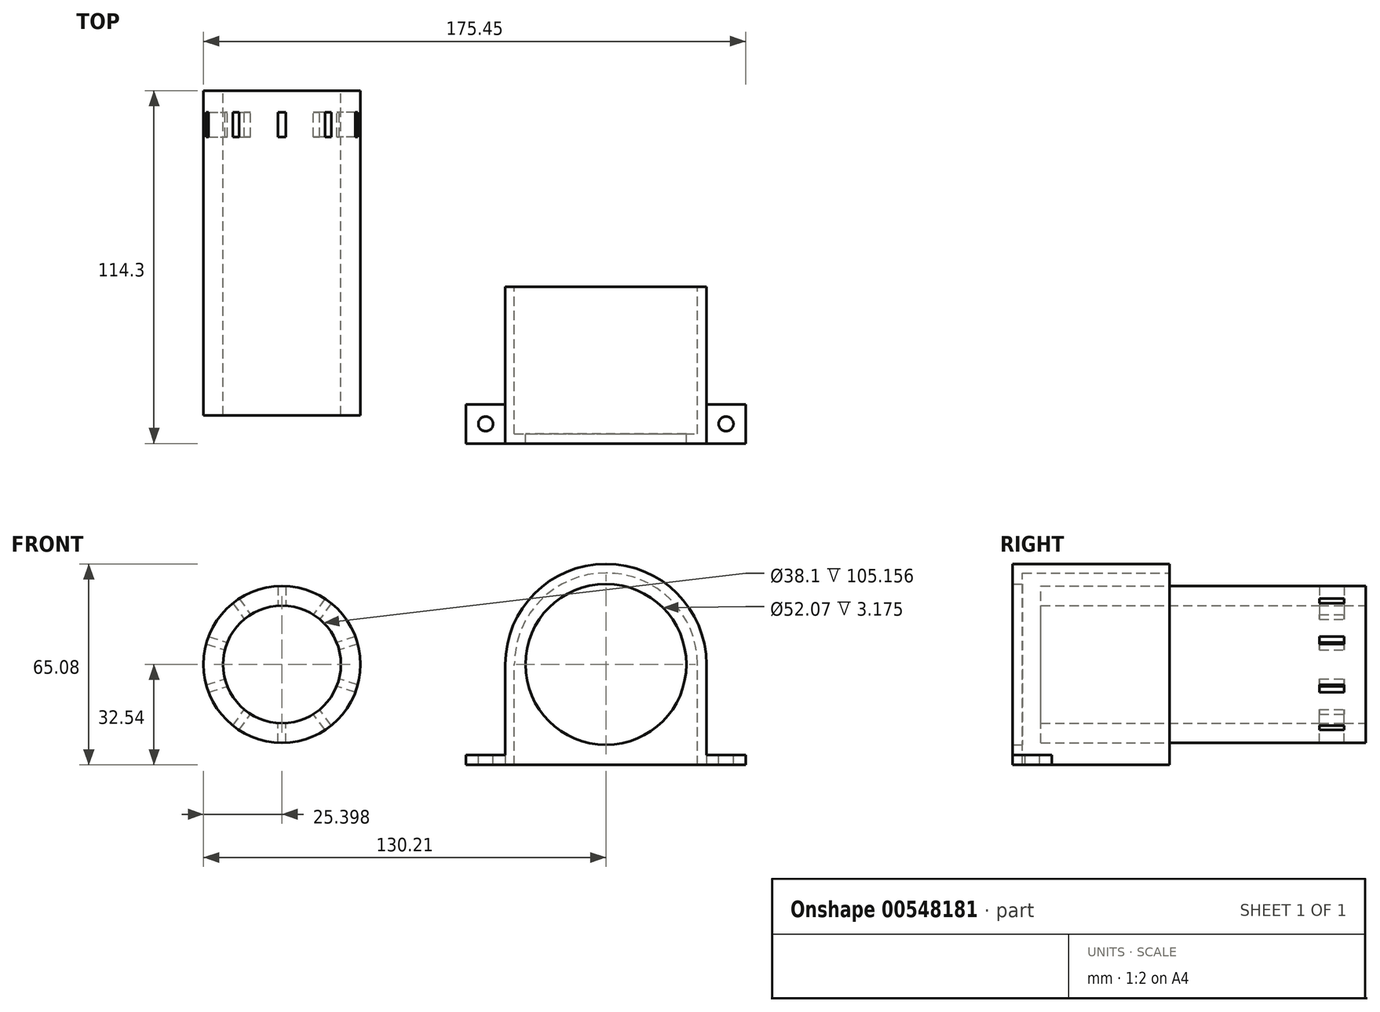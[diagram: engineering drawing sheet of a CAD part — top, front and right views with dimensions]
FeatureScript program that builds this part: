
annotation { "Feature Type Name" : "Feature", "Feature Type Description" : "" }
export const myFeature = defineFeature(function(context is Context, id is Id, definition is map)
    precondition{}
    {
        {
            var Q0;
            Q0=qCreatedBy(makeId("Front.planeOp"),FACE);
            var sketch = newSketch(context, id + "F0", { "sketchPlane" : qUnion([Q0])});
            skCircle(sketch, "E0", {"center": v(0, 0) * mm, "radius": 26.04 * mm});
            skLineSegment(sketch, "E1", {"start": v(0, -32.54) * mm, "end": v(32.54, -32.54) * mm});
            skLineSegment(sketch, "E2", {"start": v(32.54, -32.54) * mm, "end": v(32.54, 0) * mm});
            skLineSegment(sketch, "E3.MirrorCS", {"start": v(0, -32.54) * mm, "end": v(-32.54, -32.54) * mm});
            skLineSegment(sketch, "E4.MirrorCS", {"start": v(-32.54, -32.54) * mm, "end": v(-32.54, 0) * mm});
            skArc(sketch, "E5", {"start": v(32.54, 0) * mm, "mid": v(0, 32.54) * mm, "end": v(-32.54, 0) * mm});
            skSolve(sketch);
        }
        {
            var Q0;
            Q0 = qSketchRegion(id + "F0", true);
            extrude(context, id + "F1", {"entities" : qUnion([Q0]), "depth" : 114.3 * mm, "offsetDistance" : 25.4 * mm});
        }
        {
            var Q0;
            Q0=makeQuery(id+"F1.opExtrude","CAP_FACE",FACE,{"disambiguationData":[OSD([sQuery(id+"F0.wireOp",EDGE,"E0"),sQuery(id+"F0.wireOp",EDGE,"E1"),sQuery(id+"F0.wireOp",EDGE,"E2"),sQuery(id+"F0.wireOp",EDGE,"E3.MirrorCS"),sQuery(id+"F0.wireOp",EDGE,"E4.MirrorCS"),sQuery(id+"F0.wireOp",EDGE,"E5")])],"isStart":true});
            var sketch = newSketch(context, id + "F2", { "sketchPlane" : qUnion([Q0])});
            skCircle(sketch, "E6", {"center": v(0, 0) * mm, "radius": 29.62 * mm});
            skSolve(sketch);
        }
        {
            var Q0;
            Q0 = qSketchRegion(id + "F2", true);
            extrude(context, id + "F3", {"entities" : qUnion([Q0]), "operationType" : NewBodyOperationType.REMOVE, "oppositeDirection" : true, "depth" : 111.12 * mm, "offsetDistance" : 25.4 * mm});
        }
        {
            var Q0;
            Q0=makeQuery(id+"F1.opExtrude","CAP_FACE",FACE,{"disambiguationData":[OSD([sQuery(id+"F0.wireOp",EDGE,"E0"),sQuery(id+"F0.wireOp",EDGE,"E1"),sQuery(id+"F0.wireOp",EDGE,"E2"),sQuery(id+"F0.wireOp",EDGE,"E3.MirrorCS"),sQuery(id+"F0.wireOp",EDGE,"E4.MirrorCS"),sQuery(id+"F0.wireOp",EDGE,"E5")])],"isStart":true});
            var sketch = newSketch(context, id + "F4", { "sketchPlane" : qUnion([Q0])});
            skLineSegment(sketch, "E7.bottom", {"start": v(0, -50) * mm, "end": v(29.62, -50) * mm});
            skLineSegment(sketch, "E7.top", {"start": v(0, 0) * mm, "end": v(29.62, 0) * mm});
            skLineSegment(sketch, "E7.right", {"start": v(29.62, -50) * mm, "end": v(29.62, 0) * mm});
            skLineSegment(sketch, "E8.MirrorCS", {"start": v(0, 0) * mm, "end": v(-29.62, 0) * mm});
            skLineSegment(sketch, "E9.MirrorCS", {"start": v(-29.62, -50) * mm, "end": v(-29.62, 0) * mm});
            skLineSegment(sketch, "E10.MirrorCS", {"start": v(0, -50) * mm, "end": v(-29.62, -50) * mm});
            skSolve(sketch);
        }
        {
            var Q0;
            Q0 = qSketchRegion(id + "F4", true);
            extrude(context, id + "F5", {"entities" : qUnion([Q0]), "operationType" : NewBodyOperationType.REMOVE, "oppositeDirection" : true, "depth" : 111.12 * mm, "offsetDistance" : 25.4 * mm});
        }
        {
            var Q0;
            Q0=makeQuery(id+"F1.opExtrude","SWEPT_FACE",FACE,{"disambiguationData":[OSD([sQuery(id+"F0.wireOp",EDGE,"E1"),sQuery(id+"F0.wireOp",EDGE,"E3.MirrorCS")])]});
            var sketch = newSketch(context, id + "F6", { "sketchPlane" : qUnion([Q0])});
            skLineSegment(sketch, "E11.bottom", {"start": v(0, 114.3) * mm, "end": v(45.24, 114.3) * mm});
            skLineSegment(sketch, "E11.top", {"start": v(0, 101.6) * mm, "end": v(32.54, 101.6) * mm});
            skLineSegment(sketch, "E12", {"start": v(45.24, 114.3) * mm, "end": v(45.24, 101.6) * mm});
            skLineSegment(sketch, "E13", {"start": v(32.54, 101.6) * mm, "end": v(45.24, 101.6) * mm});
            skLineSegment(sketch, "E14.MirrorCS", {"start": v(0, 114.3) * mm, "end": v(-45.24, 114.3) * mm});
            skLineSegment(sketch, "E15.MirrorCS", {"start": v(-45.24, 114.3) * mm, "end": v(-45.24, 101.6) * mm});
            skLineSegment(sketch, "E16.MirrorCS", {"start": v(-32.54, 101.6) * mm, "end": v(-45.24, 101.6) * mm});
            skLineSegment(sketch, "E17.MirrorCS", {"start": v(0, 101.6) * mm, "end": v(-32.54, 101.6) * mm});
            skSolve(sketch);
        }
        {
            var Q0;
            Q0 = qSketchRegion(id + "F6", true);
            extrude(context, id + "F7", {"entities" : qUnion([Q0]), "operationType" : NewBodyOperationType.ADD, "oppositeDirection" : true, "depth" : 3.17 * mm, "offsetDistance" : 25.4 * mm});
        }
        {
            var Q0;
            Q0=makeQuery(id+"F7.boolean.opBoolean","MERGE",FACE,{"derivedFrom":[makeQuery(id+"F1.opExtrude","SWEPT_FACE",FACE,{"disambiguationData":[OSD([sQuery(id+"F0.wireOp",EDGE,"E1"),sQuery(id+"F0.wireOp",EDGE,"E3.MirrorCS")])]}),makeQuery(id+"F7.opExtrude","CAP_FACE",FACE,{"disambiguationData":[OSD([sQuery(id+"F6.wireOp",EDGE,"E11.bottom"),sQuery(id+"F6.wireOp",EDGE,"E11.top"),sQuery(id+"F6.wireOp",EDGE,"E12"),sQuery(id+"F6.wireOp",EDGE,"E13"),sQuery(id+"F6.wireOp",EDGE,"E14.MirrorCS"),sQuery(id+"F6.wireOp",EDGE,"E15.MirrorCS"),sQuery(id+"F6.wireOp",EDGE,"E16.MirrorCS"),sQuery(id+"F6.wireOp",EDGE,"E17.MirrorCS")])],"isStart":true})]});
            var sketch = newSketch(context, id + "F8", { "sketchPlane" : qUnion([Q0])});
            skLineSegment(sketch, "E18.bottom", {"start": v(-32.54, 50.8) * mm, "end": v(-45.24, 50.8) * mm});
            skLineSegment(sketch, "E18.top", {"start": v(-32.54, 63.5) * mm, "end": v(-45.24, 63.5) * mm});
            skLineSegment(sketch, "E18.left", {"start": v(-32.54, 50.8) * mm, "end": v(-32.54, 63.5) * mm});
            skLineSegment(sketch, "E18.right", {"start": v(-45.24, 50.8) * mm, "end": v(-45.24, 63.5) * mm});
            skLineSegment(sketch, "E19.MirrorCS", {"start": v(32.54, 50.8) * mm, "end": v(32.54, 63.5) * mm});
            skLineSegment(sketch, "E20.MirrorCS", {"start": v(32.54, 63.5) * mm, "end": v(45.24, 63.5) * mm});
            skLineSegment(sketch, "E21.MirrorCS", {"start": v(45.24, 50.8) * mm, "end": v(45.24, 63.5) * mm});
            skLineSegment(sketch, "E22.MirrorCS", {"start": v(32.54, 50.8) * mm, "end": v(45.24, 50.8) * mm});
            skSolve(sketch);
        }
        {
            var Q0;
            Q0 = qSketchRegion(id + "F8", true);
            extrude(context, id + "F9", {"entities" : qUnion([Q0]), "operationType" : NewBodyOperationType.ADD, "oppositeDirection" : true, "depth" : 3.17 * mm, "offsetDistance" : 25.4 * mm});
        }
        {
            var Q0;
            {var subQ0=sQuery(id+"F6.wireOp",EDGE,"E14.MirrorCS");var subQ1=sQuery(id+"F6.wireOp",EDGE,"E11.bottom");var subQ2=sQuery(id+"F0.wireOp",EDGE,"E2");var subQ3=sQuery(id+"F6.wireOp",EDGE,"E17.MirrorCS");var subQ4=sQuery(id+"F6.wireOp",EDGE,"E16.MirrorCS");var subQ5=sQuery(id+"F6.wireOp",EDGE,"E13");var subQ6=sQuery(id+"F6.wireOp",EDGE,"E11.top");var subQ7=sQuery(id+"F6.wireOp",EDGE,"E12");Q0=makeQuery(id+"F7.boolean.opBoolean","SPLIT",FACE,{"disambiguationData":[TD([makeQuery(id+"F1.opExtrude","SWEPT_FACE",FACE,{"disambiguationData":[OSD([subQ2])]})])],"derivedFrom":makeQuery(id+"F7.opExtrude","CAP_FACE",FACE,{"disambiguationData":[OSD([subQ1,subQ6,subQ7,subQ5,subQ0,sQuery(id+"F6.wireOp",EDGE,"E15.MirrorCS"),subQ4,subQ3])],"isStart":false})});}
            var sketch = newSketch(context, id + "F10", { "sketchPlane" : qUnion([Q0])});
            skCircle(sketch, "E23", {"center": v(-38.9, -57.15) * mm, "radius": 2.38 * mm});
            skCircle(sketch, "E24", {"center": v(-38.9, -107.95) * mm, "radius": 2.38 * mm});
            skCircle(sketch, "E25", {"center": v(38.9, -57.15) * mm, "radius": 2.38 * mm});
            skCircle(sketch, "E26", {"center": v(38.9, -107.95) * mm, "radius": 2.38 * mm});
            skSolve(sketch);
        }
        {
            var Q0;
            Q0 = qSketchRegion(id + "F10", true);
            extrude(context, id + "F11", {"entities" : qUnion([Q0]), "operationType" : NewBodyOperationType.REMOVE, "oppositeDirection" : true, "depth" : 25.4 * mm, "offsetDistance" : 25.4 * mm});
        }
        {
            var Q0;
            Q0=qCreatedBy(makeId("Front.planeOp"),FACE);
            var sketch = newSketch(context, id + "F12", { "sketchPlane" : qUnion([Q0])});
            skCircle(sketch, "E27", {"center": v(-104.81, 0) * mm, "radius": 25.4 * mm});
            skCircle(sketch, "E28", {"center": v(-104.81, 0) * mm, "radius": 19.05 * mm});
            skSolve(sketch);
        }
        {
            var Q0;
            Q0 = qSketchRegion(id + "F12", true);
            extrude(context, id + "F13", {"entities" : qUnion([Q0]), "depth" : 105.16 * mm, "offsetDistance" : 25.4 * mm});
        }
        {
            var Q0;
            Q0=qCreatedBy(makeId("Top.planeOp"),FACE);
            var sketch = newSketch(context, id + "F14", { "sketchPlane" : qUnion([Q0])});
            skLineSegment(sketch, "E29.bottom", {"start": v(-106.09, -7.03) * mm, "end": v(-103.55, -7.03) * mm});
            skLineSegment(sketch, "E29.top", {"start": v(-106.09, -15) * mm, "end": v(-103.55, -15) * mm});
            skLineSegment(sketch, "E29.left", {"start": v(-106.09, -7.03) * mm, "end": v(-106.09, -15) * mm});
            skLineSegment(sketch, "E29.right", {"start": v(-103.55, -7.03) * mm, "end": v(-103.55, -15) * mm});
            skSolve(sketch);
        }
        {
            var Q0;
            Q0 = qSketchRegion(id + "F14", true);
            extrude(context, id + "F15", {"entities" : qUnion([Q0]), "oppositeDirection" : true, "depth" : 32.77 * mm, "offsetDistance" : 25.4 * mm});
        }
        {
            var Q0;
            Q0=makeQuery(id+"F15.opExtrude","SWEPT_BODY",BODY,{"disambiguationData":[OSD([sQuery(id+"F14.wireOp",EDGE,"E29.bottom"),sQuery(id+"F14.wireOp",EDGE,"E29.top"),sQuery(id+"F14.wireOp",EDGE,"E29.left"),sQuery(id+"F14.wireOp",EDGE,"E29.right")])]});
            var Q1;
            Q1=makeQuery(id+"F13.opExtrude","CAP_EDGE",EDGE,{"disambiguationData":[OSD([sQuery(id+"F12.wireOp",EDGE,"E28")])],"isStart":true});
            circularPattern(context, id + "F16", {"operationType" : NewBodyOperationType.REMOVE, "entities" : qUnion([Q0]), "axis" : qUnion([Q1]), "angle" : 360 * degree, "instanceCount" : 10, "equalSpace" : true, "computeTransformsWithoutBuiltin" : true});
        }
        {
            var Q0;
            {var subQ2=sQuery(id+"F6.wireOp",EDGE,"E17.MirrorCS");var subQ3=sQuery(id+"F6.wireOp",EDGE,"E16.MirrorCS");var subQ4=sQuery(id+"F6.wireOp",EDGE,"E13");var subQ5=sQuery(id+"F6.wireOp",EDGE,"E11.top");Q0=makeQuery(id+"F7.boolean.opBoolean","SPLIT",FACE,{"disambiguationData":[TD([makeQuery(id+"F3.boolean.opBoolean","COPY",FACE,{"derivedFrom":makeQuery(id+"F3.opExtrude","CAP_FACE",FACE,{"disambiguationData":[OSD([sQuery(id+"F2.wireOp",EDGE,"E6")])],"isStart":false})})])],"derivedFrom":makeQuery(id+"F7.opExtrude","CAP_FACE",FACE,{"disambiguationData":[OSD([sQuery(id+"F6.wireOp",EDGE,"E11.bottom"),subQ5,sQuery(id+"F6.wireOp",EDGE,"E12"),subQ4,sQuery(id+"F6.wireOp",EDGE,"E14.MirrorCS"),sQuery(id+"F6.wireOp",EDGE,"E15.MirrorCS"),subQ3,subQ2])],"isStart":false})});}
            var sketch = newSketch(context, id + "F17", { "sketchPlane" : qUnion([Q0])});
            skLineSegment(sketch, "E30.bottom", {"start": v(-29.62, -111.13) * mm, "end": v(29.62, -111.13) * mm});
            skLineSegment(sketch, "E30.top", {"start": v(-29.62, -101.6) * mm, "end": v(29.62, -101.6) * mm});
            skLineSegment(sketch, "E30.left", {"start": v(-29.62, -111.13) * mm, "end": v(-29.62, -101.6) * mm});
            skLineSegment(sketch, "E30.right", {"start": v(29.62, -111.13) * mm, "end": v(29.62, -101.6) * mm});
            skSolve(sketch);
        }
        {
            var Q0;
            Q0 = qSketchRegion(id + "F17", true);
            extrude(context, id + "F18", {"entities" : qUnion([Q0]), "operationType" : NewBodyOperationType.REMOVE, "oppositeDirection" : true, "depth" : 25.4 * mm, "offsetDistance" : 25.4 * mm});
        }
        {
            var Q0;
            Q0=qCreatedBy(makeId("Top.planeOp"),FACE);
            var sketch = newSketch(context, id + "F19", { "sketchPlane" : qUnion([Q0])});
            skLineSegment(sketch, "E31.bottom", {"start": v(-61.82, 0) * mm, "end": v(71.02, 0) * mm});
            skLineSegment(sketch, "E31.top", {"start": v(-61.82, -63.5) * mm, "end": v(71.02, -63.5) * mm});
            skLineSegment(sketch, "E31.left", {"start": v(-61.82, 0) * mm, "end": v(-61.82, -63.5) * mm});
            skLineSegment(sketch, "E31.right", {"start": v(71.02, 0) * mm, "end": v(71.02, -63.5) * mm});
            skSolve(sketch);
        }
        {
            var Q0;
            Q0 = qSketchRegion(id + "F19", true);
            extrude(context, id + "F20", {"entities" : qUnion([Q0]), "operationType" : NewBodyOperationType.REMOVE, "oppositeDirection" : true, "depth" : 65.28 * mm, "offsetDistance" : 25.4 * mm, "hasSecondDirection" : true, "secondDirectionOppositeDirection" : false, "secondDirectionDepth" : 64.77 * mm});
        }
    });
